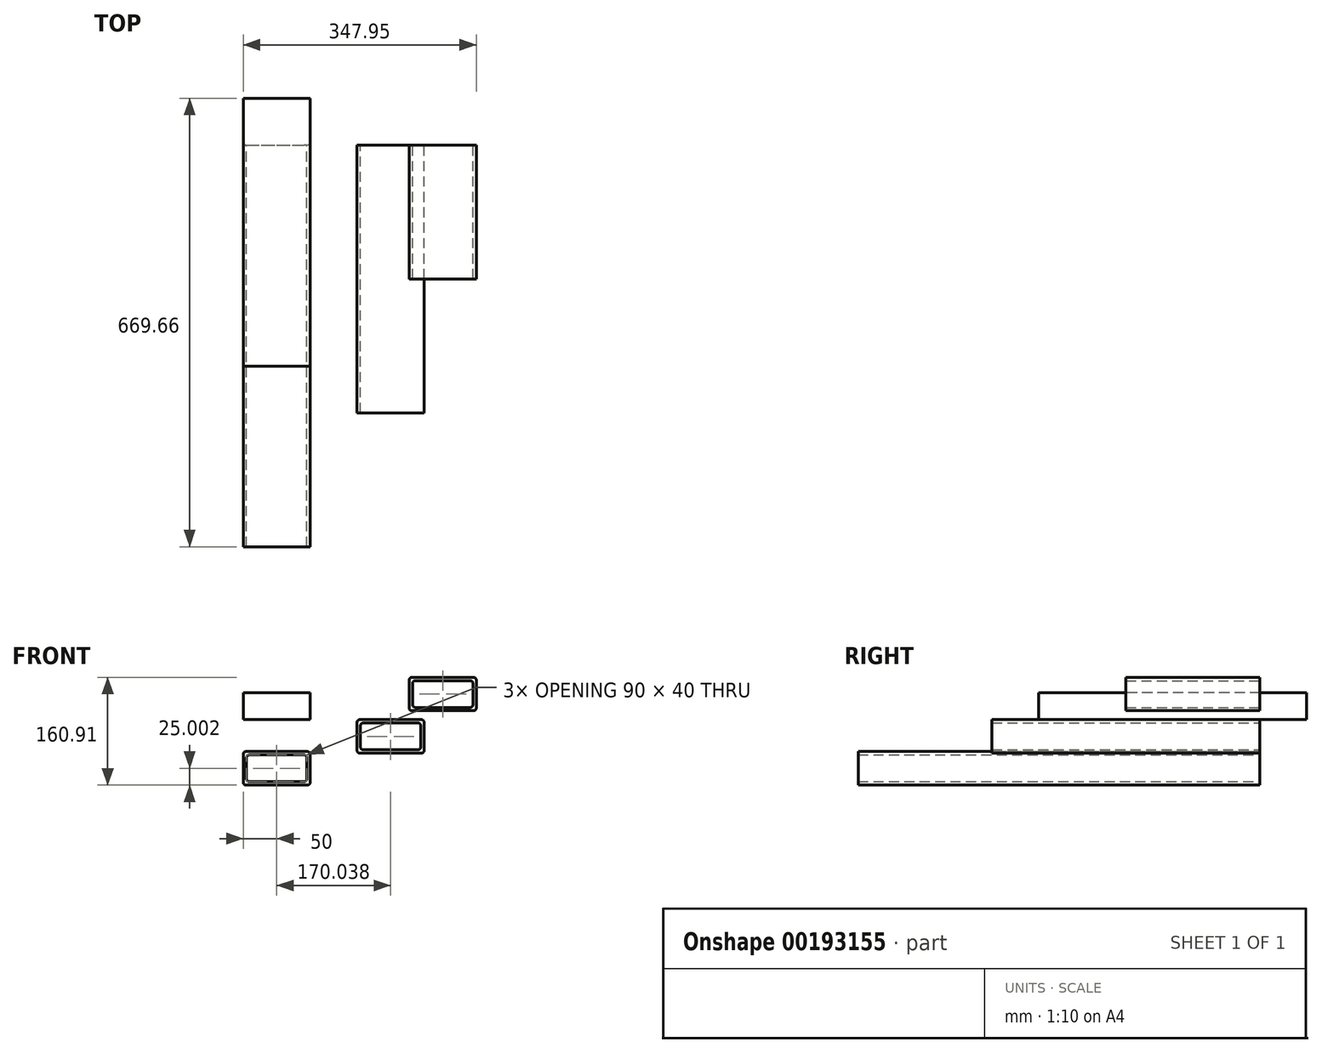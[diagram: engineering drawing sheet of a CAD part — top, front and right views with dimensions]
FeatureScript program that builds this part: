
annotation { "Feature Type Name" : "Feature", "Feature Type Description" : "" }
export const myFeature = defineFeature(function(context is Context, id is Id, definition is map)
    precondition{}
    {
        {
            var Q0;
            Q0=qCreatedBy(makeId("Top.planeOp"),FACE);
            var sketch = newSketch(context, id + "F0", { "sketchPlane" : qUnion([Q0])});
            skLineSegment(sketch, "E0.bottom", {"start": v(-74.55, 69.66) * mm, "end": v(25.45, 69.66) * mm});
            skLineSegment(sketch, "E0.top", {"start": v(-74.55, -330.34) * mm, "end": v(25.45, -330.34) * mm});
            skLineSegment(sketch, "E0.left", {"start": v(-74.55, 69.66) * mm, "end": v(-74.55, -330.34) * mm});
            skLineSegment(sketch, "E0.right", {"start": v(25.45, 69.66) * mm, "end": v(25.45, -330.34) * mm});
            skSolve(sketch);
        }
        {
            var Q0;
            Q0 = qSketchRegion(id + "F0", true);
            extrude(context, id + "F1", {"entities" : qUnion([Q0]), "depth" : 40 * mm});
        }
        {
            var Q0;
            Q0=qCreatedBy(makeId("Front.planeOp"),FACE);
            var sketch = newSketch(context, id + "F2", { "sketchPlane" : qUnion([Q0])});
            skLineSegment(sketch, "E1.bottom", {"start": v(-70.57, -48.12) * mm, "end": v(21.43, -48.12) * mm});
            skLineSegment(sketch, "E1.top", {"start": v(-70.57, -98.12) * mm, "end": v(21.43, -98.12) * mm});
            skLineSegment(sketch, "E1.left", {"start": v(-74.57, -52.12) * mm, "end": v(-74.57, -94.12) * mm});
            skLineSegment(sketch, "E1.right", {"start": v(25.43, -52.12) * mm, "end": v(25.43, -94.12) * mm});
            skLineSegment(sketch, "E2.bottom", {"start": v(-65.57, -53.12) * mm, "end": v(16.43, -53.12) * mm});
            skLineSegment(sketch, "E2.top", {"start": v(-65.57, -93.12) * mm, "end": v(16.43, -93.12) * mm});
            skLineSegment(sketch, "E2.left", {"start": v(-69.57, -57.12) * mm, "end": v(-69.57, -89.12) * mm});
            skLineSegment(sketch, "E2.right", {"start": v(20.43, -57.12) * mm, "end": v(20.43, -89.12) * mm});
            skPoint(sketch, "E3.visualSharp", {"position": v(-74.57, -48.12) * mm});
            skArc(sketch, "E3.filletArc", {"start": v(-70.57, -48.12) * mm, "mid": v(-73.4, -49.29) * mm, "end": v(-74.57, -52.12) * mm});
            skPoint(sketch, "E4.visualSharp", {"position": v(25.43, -48.12) * mm});
            skArc(sketch, "E4.filletArc", {"start": v(25.43, -52.12) * mm, "mid": v(24.26, -49.29) * mm, "end": v(21.43, -48.12) * mm});
            skPoint(sketch, "E5.visualSharp", {"position": v(25.43, -98.12) * mm});
            skArc(sketch, "E5.filletArc", {"start": v(21.43, -98.12) * mm, "mid": v(24.26, -96.95) * mm, "end": v(25.43, -94.12) * mm});
            skPoint(sketch, "E6.visualSharp", {"position": v(-74.57, -98.12) * mm});
            skArc(sketch, "E6.filletArc", {"start": v(-74.57, -94.12) * mm, "mid": v(-73.4, -96.95) * mm, "end": v(-70.57, -98.12) * mm});
            skPoint(sketch, "E7.visualSharp", {"position": v(20.43, -93.12) * mm});
            skArc(sketch, "E7.filletArc", {"start": v(16.43, -93.12) * mm, "mid": v(19.26, -91.95) * mm, "end": v(20.43, -89.12) * mm});
            skPoint(sketch, "E8.visualSharp", {"position": v(20.43, -53.12) * mm});
            skArc(sketch, "E8.filletArc", {"start": v(20.43, -57.12) * mm, "mid": v(19.26, -54.29) * mm, "end": v(16.43, -53.12) * mm});
            skPoint(sketch, "E9.visualSharp", {"position": v(-69.57, -53.12) * mm});
            skArc(sketch, "E9.filletArc", {"start": v(-65.57, -53.12) * mm, "mid": v(-68.4, -54.29) * mm, "end": v(-69.57, -57.12) * mm});
            skPoint(sketch, "E10.visualSharp", {"position": v(-69.57, -93.12) * mm});
            skArc(sketch, "E10.filletArc", {"start": v(-69.57, -89.12) * mm, "mid": v(-68.4, -91.95) * mm, "end": v(-65.57, -93.12) * mm});
            skSolve(sketch);
        }
        {
            var Q0;
            Q0 = qSketchRegion(id + "F2", true);
            extrude(context, id + "F3", {"entities" : qUnion([Q0]), "depth" : 600 * mm});
        }
        {
            var Q0;
            Q0=qCreatedBy(makeId("Front.planeOp"),FACE);
            var sketch = newSketch(context, id + "F4", { "sketchPlane" : qUnion([Q0])});
            skLineSegment(sketch, "E11.bottom", {"start": v(99.47, -0.41) * mm, "end": v(191.47, -0.41) * mm});
            skLineSegment(sketch, "E11.top", {"start": v(99.47, -50.41) * mm, "end": v(191.47, -50.41) * mm});
            skLineSegment(sketch, "E11.left", {"start": v(95.47, -4.41) * mm, "end": v(95.47, -46.41) * mm});
            skLineSegment(sketch, "E11.right", {"start": v(195.47, -4.41) * mm, "end": v(195.47, -46.41) * mm});
            skLineSegment(sketch, "E12.bottom", {"start": v(104.47, -5.41) * mm, "end": v(186.47, -5.41) * mm});
            skLineSegment(sketch, "E12.top", {"start": v(104.47, -45.41) * mm, "end": v(186.47, -45.41) * mm});
            skLineSegment(sketch, "E12.left", {"start": v(100.47, -9.41) * mm, "end": v(100.47, -41.41) * mm});
            skLineSegment(sketch, "E12.right", {"start": v(190.47, -9.41) * mm, "end": v(190.47, -41.41) * mm});
            skPoint(sketch, "E13.visualSharp", {"position": v(95.47, -0.41) * mm});
            skArc(sketch, "E13.filletArc", {"start": v(99.47, -0.41) * mm, "mid": v(96.64, -1.59) * mm, "end": v(95.47, -4.41) * mm});
            skPoint(sketch, "E14.visualSharp", {"position": v(195.47, -0.41) * mm});
            skArc(sketch, "E14.filletArc", {"start": v(195.47, -4.41) * mm, "mid": v(194.3, -1.59) * mm, "end": v(191.47, -0.41) * mm});
            skPoint(sketch, "E15.visualSharp", {"position": v(195.47, -50.41) * mm});
            skArc(sketch, "E15.filletArc", {"start": v(191.47, -50.41) * mm, "mid": v(194.3, -49.24) * mm, "end": v(195.47, -46.41) * mm});
            skPoint(sketch, "E16.visualSharp", {"position": v(95.47, -50.41) * mm});
            skArc(sketch, "E16.filletArc", {"start": v(95.47, -46.41) * mm, "mid": v(96.64, -49.24) * mm, "end": v(99.47, -50.41) * mm});
            skPoint(sketch, "E17.visualSharp", {"position": v(190.47, -45.41) * mm});
            skArc(sketch, "E17.filletArc", {"start": v(186.47, -45.41) * mm, "mid": v(189.3, -44.24) * mm, "end": v(190.47, -41.41) * mm});
            skPoint(sketch, "E18.visualSharp", {"position": v(190.47, -5.41) * mm});
            skArc(sketch, "E18.filletArc", {"start": v(190.47, -9.41) * mm, "mid": v(189.3, -6.59) * mm, "end": v(186.47, -5.41) * mm});
            skPoint(sketch, "E19.visualSharp", {"position": v(100.47, -5.41) * mm});
            skArc(sketch, "E19.filletArc", {"start": v(104.47, -5.41) * mm, "mid": v(101.64, -6.59) * mm, "end": v(100.47, -9.41) * mm});
            skPoint(sketch, "E20.visualSharp", {"position": v(100.47, -45.41) * mm});
            skArc(sketch, "E20.filletArc", {"start": v(100.47, -41.41) * mm, "mid": v(101.64, -44.24) * mm, "end": v(104.47, -45.41) * mm});
            skSolve(sketch);
        }
        {
            var Q0;
            Q0 = qSketchRegion(id + "F4", true);
            extrude(context, id + "F5", {"entities" : qUnion([Q0]), "depth" : 400 * mm});
        }
        {
            var Q0;
            Q0=qCreatedBy(makeId("Front.planeOp"),FACE);
            var sketch = newSketch(context, id + "F6", { "sketchPlane" : qUnion([Q0])});
            skLineSegment(sketch, "E21.bottom", {"start": v(177.38, 62.79) * mm, "end": v(269.38, 62.79) * mm});
            skLineSegment(sketch, "E21.top", {"start": v(177.38, 12.79) * mm, "end": v(269.38, 12.79) * mm});
            skLineSegment(sketch, "E21.left", {"start": v(173.38, 58.79) * mm, "end": v(173.38, 16.79) * mm});
            skLineSegment(sketch, "E21.right", {"start": v(273.38, 58.79) * mm, "end": v(273.38, 16.79) * mm});
            skLineSegment(sketch, "E22.bottom", {"start": v(182.38, 57.79) * mm, "end": v(264.38, 57.79) * mm});
            skLineSegment(sketch, "E22.top", {"start": v(182.38, 17.79) * mm, "end": v(264.38, 17.79) * mm});
            skLineSegment(sketch, "E22.left", {"start": v(178.38, 53.79) * mm, "end": v(178.38, 21.79) * mm});
            skLineSegment(sketch, "E22.right", {"start": v(268.38, 53.79) * mm, "end": v(268.38, 21.79) * mm});
            skPoint(sketch, "E23.visualSharp", {"position": v(173.38, 62.79) * mm});
            skArc(sketch, "E23.filletArc", {"start": v(177.38, 62.79) * mm, "mid": v(174.55, 61.61) * mm, "end": v(173.38, 58.79) * mm});
            skPoint(sketch, "E24.visualSharp", {"position": v(273.38, 62.79) * mm});
            skArc(sketch, "E24.filletArc", {"start": v(273.38, 58.79) * mm, "mid": v(272.2, 61.61) * mm, "end": v(269.38, 62.79) * mm});
            skPoint(sketch, "E25.visualSharp", {"position": v(273.38, 12.79) * mm});
            skArc(sketch, "E25.filletArc", {"start": v(269.38, 12.79) * mm, "mid": v(272.2, 13.96) * mm, "end": v(273.38, 16.79) * mm});
            skPoint(sketch, "E26.visualSharp", {"position": v(173.38, 12.79) * mm});
            skArc(sketch, "E26.filletArc", {"start": v(173.38, 16.79) * mm, "mid": v(174.55, 13.96) * mm, "end": v(177.38, 12.79) * mm});
            skPoint(sketch, "E27.visualSharp", {"position": v(268.38, 17.79) * mm});
            skArc(sketch, "E27.filletArc", {"start": v(264.38, 17.79) * mm, "mid": v(267.2, 18.96) * mm, "end": v(268.38, 21.79) * mm});
            skPoint(sketch, "E28.visualSharp", {"position": v(268.38, 57.79) * mm});
            skArc(sketch, "E28.filletArc", {"start": v(268.38, 53.79) * mm, "mid": v(267.2, 56.61) * mm, "end": v(264.38, 57.79) * mm});
            skPoint(sketch, "E29.visualSharp", {"position": v(178.38, 57.79) * mm});
            skArc(sketch, "E29.filletArc", {"start": v(182.38, 57.79) * mm, "mid": v(179.55, 56.61) * mm, "end": v(178.38, 53.79) * mm});
            skPoint(sketch, "E30.visualSharp", {"position": v(178.38, 17.79) * mm});
            skArc(sketch, "E30.filletArc", {"start": v(178.38, 21.79) * mm, "mid": v(179.55, 18.96) * mm, "end": v(182.38, 17.79) * mm});
            skSolve(sketch);
        }
        {
            var Q0;
            Q0 = qSketchRegion(id + "F6", true);
            extrude(context, id + "F7", {"entities" : qUnion([Q0]), "depth" : 200 * mm});
        }
    });
